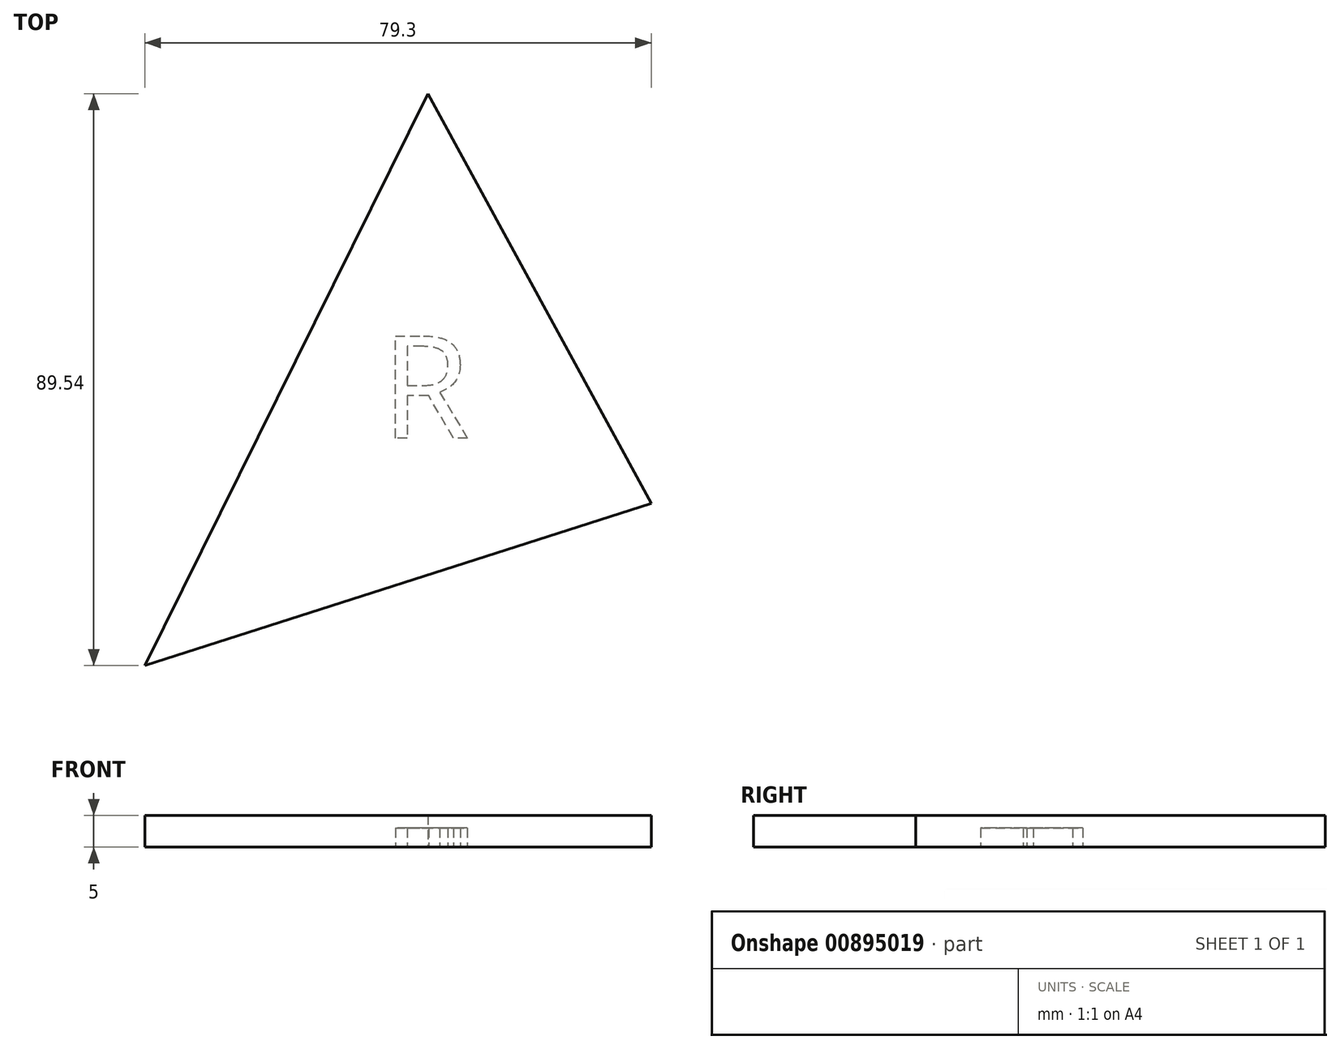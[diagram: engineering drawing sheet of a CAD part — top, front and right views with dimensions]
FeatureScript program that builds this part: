
annotation { "Feature Type Name" : "Feature", "Feature Type Description" : "" }
export const myFeature = defineFeature(function(context is Context, id is Id, definition is map)
    precondition{}
    {
        {
            var Q0;
            Q0=qCreatedBy(makeId("Top.planeOp"),FACE);
            var sketch = newSketch(context, id + "F0", { "sketchPlane" : qUnion([Q0])});
            skLineSegment(sketch, "E0", {"start": v(-5.82, 37.16) * mm, "end": v(-50.93, -54.01) * mm});
            skLineSegment(sketch, "E1", {"start": v(-6.62, 35.53) * mm, "end": v(28.37, -28.6) * mm});
            skLineSegment(sketch, "E2", {"start": v(-50.93, -54.01) * mm, "end": v(28.37, -28.6) * mm});
            skSolve(sketch);
        }
        {
            var Q0;
            {var subQ2=sQuery(id+"F0.wireOp",EDGE,"E1");Q0=makeQuery(id+"F0.imprint","IMPRINT",FACE,{"disambiguationData":[TD([[makeQuery(id+"F0.imprint","IMPRINT",EDGE,{"derivedFrom":subQ2}),-1.0]])]});}
            extrude(context, id + "F1", {"entities" : qUnion([Q0]), "depth" : 5 * mm, "offsetDistance" : 25.4 * mm});
        }
        {
            var Q0;
            Q0=qCreatedBy(makeId("Top.planeOp"),FACE);
            var sketch = newSketch(context, id + "F2", { "sketchPlane" : qUnion([Q0])});
            skCircle(sketch, "E3", {"center": v(-6.77, 38.34) * mm, "radius": 2.52 * mm});
            skCircle(sketch, "E4", {"center": v(-6.77, 38.34) * mm, "radius": 1.52 * mm});
            skCircle(sketch, "E5", {"center": v(-6.77, 38.34) * mm, "radius": 2.19 * mm});
            skSolve(sketch);
        }
        {
            var Q0;
            Q0=sQuery(id+"F2.wireOp",EDGE,"E3");
            extrude(context, id + "F3", {"bodyType" : ToolBodyType.SURFACE, "surfaceEntities" : qUnion([Q0]), "depth" : 5 * mm, "offsetDistance" : 25.4 * mm});
        }
        {
            var Q0;
            Q0=qCreatedBy(makeId("Top.planeOp"),FACE);
            var sketch = newSketch(context, id + "F4", { "sketchPlane" : qUnion([Q0])});
            skLineSegment(sketch, "E6", {"start": v(-7, 19.82) * mm, "end": v(-41.67, -46.18) * mm});
            skLineSegment(sketch, "E7", {"start": v(-41.67, -46.18) * mm, "end": v(16.74, -24.57) * mm});
            skLineSegment(sketch, "E8", {"start": v(-7, 19.82) * mm, "end": v(16.74, -24.57) * mm});
            skSolve(sketch);
        }
        {
            var Q0;
            Q0 = qSketchRegion(id + "F4", true);
            extrude(context, id + "F5", {"entities" : qUnion([Q0]), "operationType" : NewBodyOperationType.ADD, "depth" : 3 * mm, "offsetDistance" : 25.4 * mm});
        }
        {
            var Q0;
            Q0=qCreatedBy(makeId("Top.planeOp"),FACE);
            var sketch = newSketch(context, id + "F6", { "sketchPlane" : qUnion([Q0])});
            skText(sketch, "E9", { "text": "R", "fontName": "OpenSans-Regular.ttf"});
            const initialGuessF6  = {"E9": [-0.01389, -0.0184, 1, 0, 0.01614]};
            skSetInitialGuess(sketch, initialGuessF6);
            skSolve(sketch);
        }
        {
            var Q0;
            Q0 = qSketchRegion(id + "F6", true);
            extrude(context, id + "F7", {"entities" : qUnion([Q0]), "operationType" : NewBodyOperationType.REMOVE, "depth" : 3 * mm, "offsetDistance" : 25.4 * mm});
        }
        {
            var Q0;
            Q0 = qSketchRegion(id + "F6", true);
            extrude(context, id + "F8", {"entities" : qUnion([Q0]), "operationType" : NewBodyOperationType.REMOVE, "endBound" : BoundingType.THROUGH_ALL, "oppositeDirection" : true, "depth" : 25.4 * mm, "offsetDistance" : 25.4 * mm});
        }
    });
